# Revit family: Boiler-Gas-Weil-McLain-SVF_725-850
name_source: partatom
category: Mechanical Equipment
units: mm (PartAtom-declared; Revit-internal decimal feet)

## family parameters
Always vertical = Yes
Cut with Voids When Loaded = No
OmniClass Number = 23.75.10.11.14
OmniClass Title = Hot Water Heat Generators
Part Type = Normal
Room Calculation Point = No
Round Connector Dimension = Use Diameter
Shared = No
Work Plane-Based = Yes

## types (2) — shared parameters
Assembly Code = D3020100
Boiler Return Water Diameter = 3"
Boiler Supply Water Diameter = 3"
Condensate Drain Connection Diameter = 1"
CondensateCL = 0' - 4"
CondensateLocate = 0' - 10 1/4"
Dead Weight = 2020
Default Elevation = 0' - 0"
Flue Diameter = 6"
Flue Locate = 6' - 5 9/16"
FlueHolderDia = 0' - 7 1/2"
Frame Accent Material = Plastic - WeilMcLain - Black
Frame Finish = Metal - WeilMcLain - Gray
Frequency = 60 Hz
Fuel Type = Natural Gas
Full Load Current = 23 A
Gas Connection Diameter = 1"
Gas Connection Type = Female NPT
Height = 4' - 1 13/16"
Keynote = 23 52 00
Length = 3' - 6 3/16"
Manufacturer = Weil-McLain
Number of Poles = 1
Operating Temperature = 40 - 120 F
Operating Weight = 3000
Phase = 1
Product Page URL = https://www.weil-mclain.com
Screen Material = Plastic - WeilMcLain - Blue
Standards Conformance = ASME  ;  AHRI  ;  CSA
Supply Air Connection Diameter = 6"
Tank Capacity = 118 gal
Type Comments = No Side Clearance. Side-by-Side install capable.
URL = https://www.weil-mclain.com
Voltage = 120 V
Water Connection Type = Class 150 ASME Flange
Width = 2' - 0 29/32"

## per-type parameters (varying)
| type | Description | Flue Inset | Model | Net AHRI MBH | Product Name | Thermal Efficiency | Total Heating Capacity |
| SVP 725 | Weil-McLain Commercial NG Gas Boiler - SVF 725 as Specified | 1' - 0 7/32" | SVF 725 | 616.0 Btu/h | SVF 725 | 97.7 | 708.0 Btu/h |
| SVP 850 | Weil-McLain Commercial NG Gas Boiler - SVF850 as Specified | 1' - 5 3/8" | SVF850 | 721.0 Btu/h | SVF850 Boiler | 97.5 | 829.0 Btu/h |

## geometry (parser evidence)
native form markers: Sweep x2
no freeform markers — native parametric forms only
